# Revit family: PipeAccessories_Valve-Balancing_TA-Hydronics_STAP_DN15-50
name_source: partatom
category: Pipe Accessories
units: mm (PartAtom-declared; Revit-internal decimal feet)

## family parameters
Always vertical = Yes
Cut with Voids When Loaded = No
OmniClass Number = 23.65.55.14.17
OmniClass Title = Adjusting/Controlling Valves for Liquid Services
Part Type = Valve - Breaks Into
Round Connector Dimension = Use Diameter
Shared = No
Work Plane-Based = No

## types (1)
- TA-Hydronics_STAP_DN15-50
    BodyMaterial = TA-Hydronics_Ametal
    ConnectorDescription = DN 15-50: Flanges according to EN-1092-2.
    Description = Differential pressure controllers valve
    DrainKitAngle = 50°
    DrainKitDiameter = 8 mm  [stored 0.0262467 ft]
    DrainKitLength = 70 mm  [stored 0.229659 ft]
    HandleMaterial = TA-Hydronics_Polyamide
    LeverDiameter = 20 mm  [stored 0.0656168 ft]
    LeverPosition = 8.32 mm
    LeverThickness = 12 mm  [stored 0.0393701 ft]
    Lookup Table Name = PipeAccessories_Valve-Balancing_TA-Hydronics_STAP_DN15-50
    Manufacturer = Tour&Andersson
    Max.WorkingTemperature = 120°C
    Min.WorkingTemperature = -20°C
    Model = STAP
    ModifiedIssue_ANZRS = 20141016.54 $
    SpindleAngle = 78°
    SpindleConnectionPosition = 20 mm  [stored 0.0656168 ft]
    Type Comments = Screwed ends
    URL = http://www.tahydronics.com

note: [stored X ft] marks values corroborated as IEEE doubles in the binary element streams (Revit-internal decimal feet)

## geometry (parser evidence)
native form markers: Sweep x3
no freeform markers — native parametric forms only
